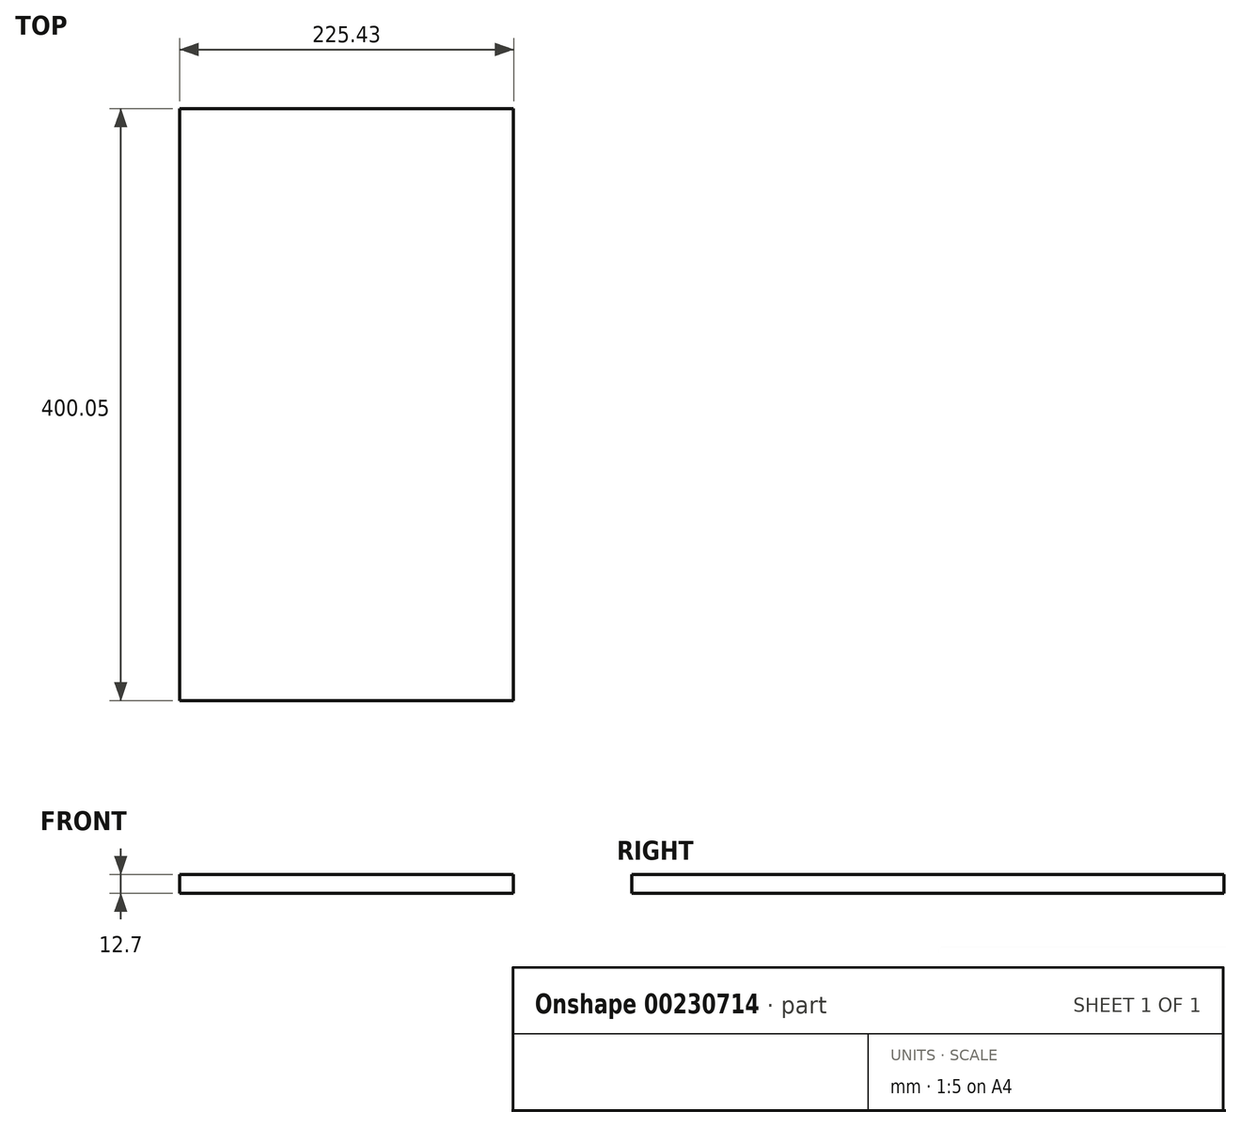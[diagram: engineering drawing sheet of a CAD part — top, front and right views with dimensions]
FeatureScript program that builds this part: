
annotation { "Feature Type Name" : "Feature", "Feature Type Description" : "" }
export const myFeature = defineFeature(function(context is Context, id is Id, definition is map)
    precondition{}
    {
        {
            var Q0;
            Q0=qCreatedBy(makeId("Front.planeOp"),FACE);
            var sketch = newSketch(context, id + "F0", { "sketchPlane" : qUnion([Q0])});
            skLineSegment(sketch, "E0.bottom", {"start": v(-53.4, 2.24) * mm, "end": v(172.03, 2.24) * mm});
            skLineSegment(sketch, "E0.top", {"start": v(-53.4, -10.46) * mm, "end": v(172.03, -10.46) * mm});
            skLineSegment(sketch, "E0.left", {"start": v(-53.4, 2.24) * mm, "end": v(-53.4, -10.46) * mm});
            skLineSegment(sketch, "E0.right", {"start": v(172.03, 2.24) * mm, "end": v(172.03, -10.46) * mm});
            skSolve(sketch);
        }
        {
            var Q0;
            Q0=makeQuery(id+"F0.imprint","IMPRINT",FACE,{"disambiguationData":[TD([[makeQuery(id+"F0.imprint","IMPRINT",EDGE,{"derivedFrom":sQuery(id+"F0.wireOp",EDGE,"E0.bottom")}),-1.0]])]});
            extrude(context, id + "F1", {"entities" : qUnion([Q0]), "oppositeDirection" : true, "depth" : 400.05 * mm});
        }
    });
